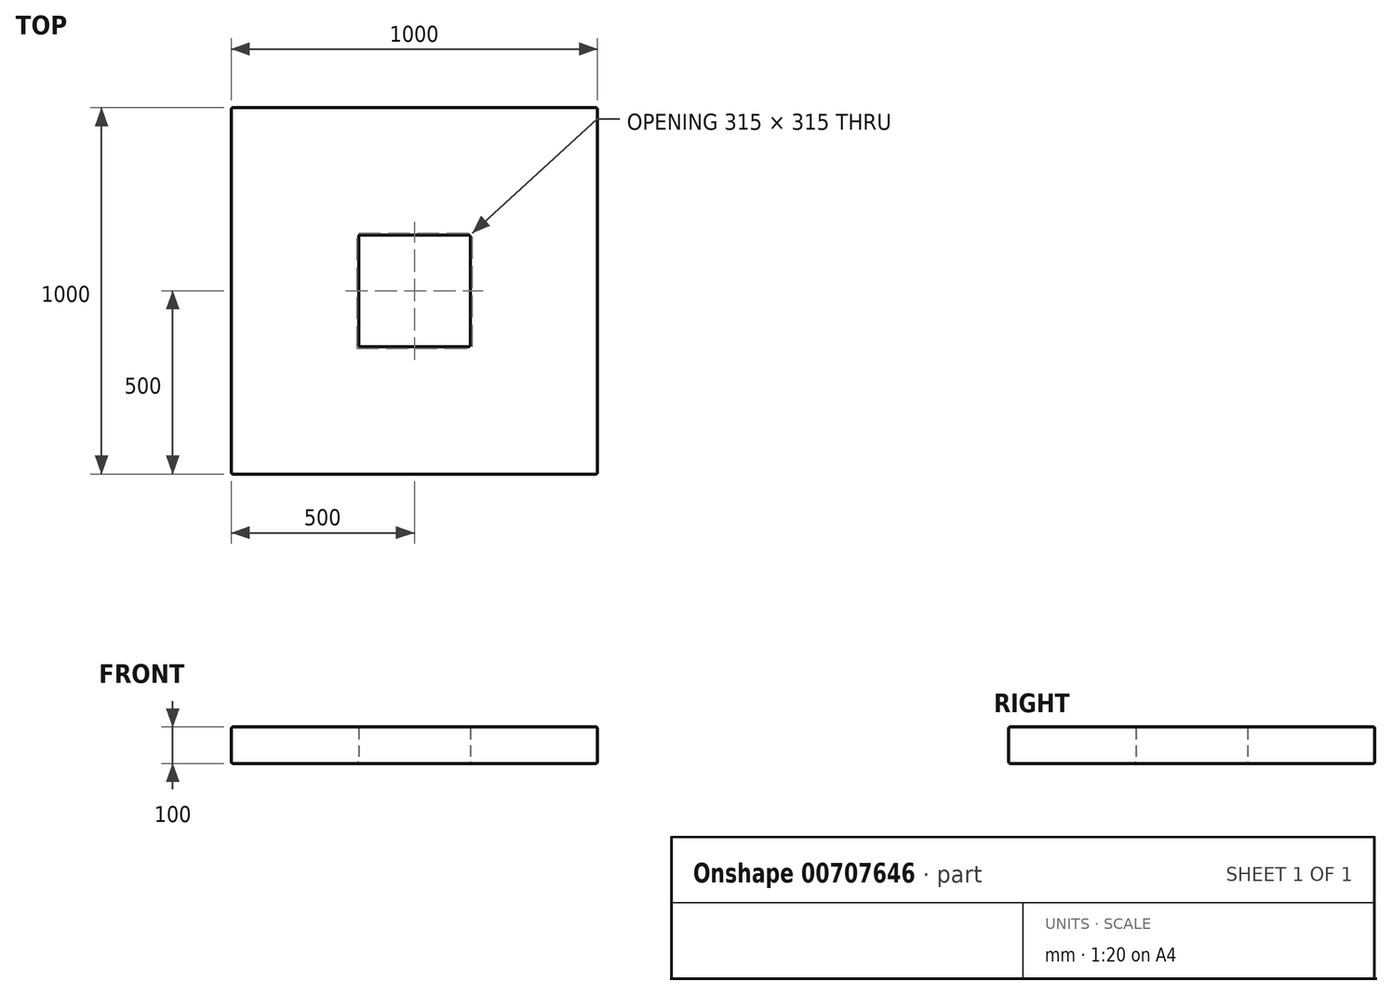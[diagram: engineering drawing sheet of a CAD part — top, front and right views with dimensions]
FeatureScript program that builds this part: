
annotation { "Feature Type Name" : "Feature", "Feature Type Description" : "" }
export const myFeature = defineFeature(function(context is Context, id is Id, definition is map)
    precondition{}
    {
        {
            var Q0;
            Q0=qCreatedBy(makeId("Top.planeOp"),FACE);
            var sketch = newSketch(context, id + "F0", { "sketchPlane" : qUnion([Q0])});
            skLineSegment(sketch, "E0.bottom", {"start": v(500, 500) * mm, "end": v(-500, 500) * mm});
            skLineSegment(sketch, "E0.top", {"start": v(500, -500) * mm, "end": v(-500, -500) * mm});
            skLineSegment(sketch, "E0.left", {"start": v(500, 500) * mm, "end": v(500, -500) * mm});
            skLineSegment(sketch, "E0.right", {"start": v(-500, 500) * mm, "end": v(-500, -500) * mm});
            skPoint(sketch, "E0.middle", {"position": v(0, 0) * mm});
            skLineSegment(sketch, "E1.bottom", {"start": v(152.5, 152.5) * mm, "end": v(-152.5, 152.5) * mm});
            skLineSegment(sketch, "E1.top", {"start": v(152.5, -152.5) * mm, "end": v(-152.5, -152.5) * mm});
            skLineSegment(sketch, "E1.left", {"start": v(152.5, 152.5) * mm, "end": v(152.5, -152.5) * mm});
            skLineSegment(sketch, "E1.right", {"start": v(-152.5, 152.5) * mm, "end": v(-152.5, -152.5) * mm});
            skSolve(sketch);
        }
        {
            var Q0;
            Q0=makeQuery(id+"F0.imprint","IMPRINT",FACE,{"disambiguationData":[TD([[makeQuery(id+"F0.imprint","IMPRINT",EDGE,{"derivedFrom":sQuery(id+"F0.wireOp",EDGE,"E0.bottom")}),1.0]])]});
            extrude(context, id + "F1", {"entities" : qUnion([Q0]), "depth" : 100 * mm, "offsetDistance" : 25 * mm});
        }
        {
            var Q0;
            Q0=makeQuery(id+"F1.opExtrude","CAP_FACE",FACE,{"disambiguationData":[OSD([sQuery(id+"F0.wireOp",EDGE,"E0.bottom"),sQuery(id+"F0.wireOp",EDGE,"E0.top"),sQuery(id+"F0.wireOp",EDGE,"E0.left"),sQuery(id+"F0.wireOp",EDGE,"E0.right"),sQuery(id+"F0.wireOp",EDGE,"E1.bottom"),sQuery(id+"F0.wireOp",EDGE,"E1.top"),sQuery(id+"F0.wireOp",EDGE,"E1.left"),sQuery(id+"F0.wireOp",EDGE,"E1.right")])],"isStart":false});
            var Q1;
            Q1=makeQuery(id+"F1.opExtrude","CAP_FACE",FACE,{"disambiguationData":[OSD([sQuery(id+"F0.wireOp",EDGE,"E0.bottom"),sQuery(id+"F0.wireOp",EDGE,"E0.top"),sQuery(id+"F0.wireOp",EDGE,"E0.left"),sQuery(id+"F0.wireOp",EDGE,"E0.right"),sQuery(id+"F0.wireOp",EDGE,"E1.bottom"),sQuery(id+"F0.wireOp",EDGE,"E1.top"),sQuery(id+"F0.wireOp",EDGE,"E1.left"),sQuery(id+"F0.wireOp",EDGE,"E1.right")])],"isStart":true});
            var Q2;
            Q2=makeQuery(id+"F1.opExtrude","SWEPT_FACE",FACE,{"disambiguationData":[OSD([sQuery(id+"F0.wireOp",EDGE,"E1.bottom")])]});
            var Q3;
            Q3=makeQuery(id+"F1.opExtrude","CAP_EDGE",EDGE,{"disambiguationData":[OSD([sQuery(id+"F0.wireOp",EDGE,"E1.right")])],"isStart":true});
            var Q4;
            Q4=makeQuery(id+"F1.opExtrude","SWEPT_FACE",FACE,{"disambiguationData":[OSD([sQuery(id+"F0.wireOp",EDGE,"E1.left")])]});
            var Q5;
            Q5=makeQuery(id+"F1.opExtrude","SWEPT_FACE",FACE,{"disambiguationData":[OSD([sQuery(id+"F0.wireOp",EDGE,"E1.top")])]});
            var Q6;
            Q6=makeQuery(id+"F1.opExtrude","SWEPT_FACE",FACE,{"disambiguationData":[OSD([sQuery(id+"F0.wireOp",EDGE,"E0.bottom")])]});
            var Q7;
            Q7=makeQuery(id+"F1.opExtrude","SWEPT_FACE",FACE,{"disambiguationData":[OSD([sQuery(id+"F0.wireOp",EDGE,"E0.top")])]});
            fillet(context, id + "F2", {"entities" : qUnion([Q0, Q1, Q2, Q3, Q4, Q5, Q6, Q7]), "radius" : 5 * mm, "tangentPropagation" : true, "allowEdgeOverflow" : false});
        }
    });
